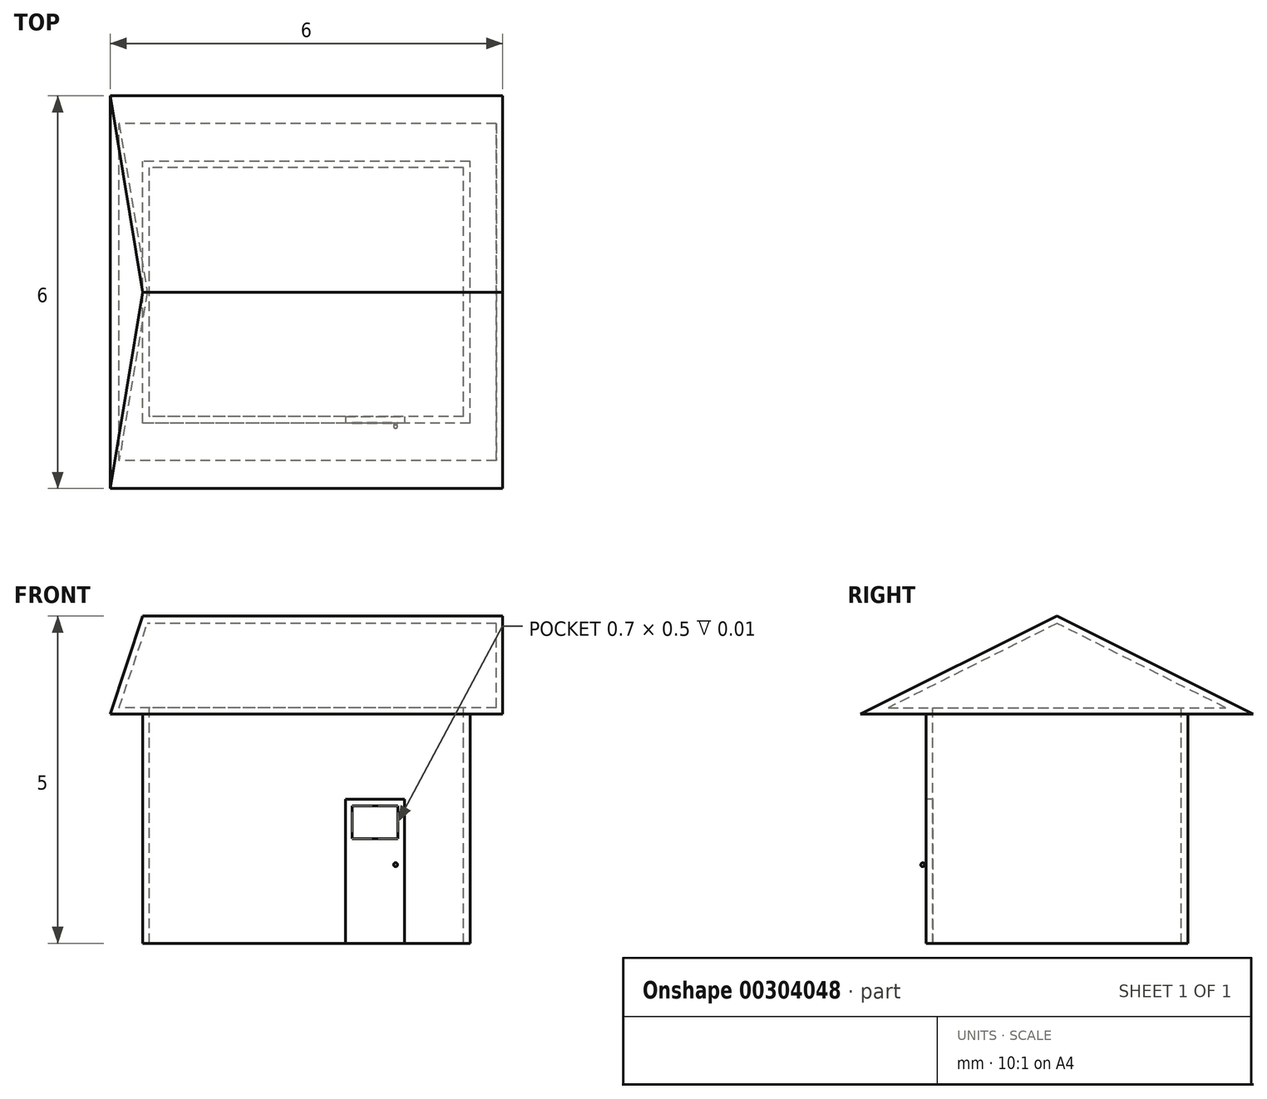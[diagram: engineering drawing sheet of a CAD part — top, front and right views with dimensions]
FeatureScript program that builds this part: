
annotation { "Feature Type Name" : "Feature", "Feature Type Description" : "" }
export const myFeature = defineFeature(function(context is Context, id is Id, definition is map)
    precondition{}
    {
        {
            var Q0;
            Q0=qCreatedBy(makeId("Front.planeOp"),FACE);
            var sketch = newSketch(context, id + "F0", { "sketchPlane" : qUnion([Q0])});
            skLineSegment(sketch, "E0.bottom", {"start": v(2.5, 0) * mm, "end": v(-2.5, 0) * mm});
            skLineSegment(sketch, "E0.top", {"start": v(2.5, 3.5) * mm, "end": v(-2.5, 3.5) * mm});
            skLineSegment(sketch, "E0.left", {"start": v(2.5, 0) * mm, "end": v(2.5, 3.5) * mm});
            skLineSegment(sketch, "E0.right", {"start": v(-2.5, 0) * mm, "end": v(-2.5, 3.5) * mm});
            skPoint(sketch, "E0.middle", {"position": v(0, 1.75) * mm});
            skSolve(sketch);
        }
        {
            var Q0;
            Q0=makeQuery(id+"F0.imprint","IMPRINT",FACE,{"disambiguationData":[TD([[makeQuery(id+"F0.imprint","IMPRINT",EDGE,{"derivedFrom":sQuery(id+"F0.wireOp",EDGE,"E0.bottom")}),-1.0]])]});
            extrude(context, id + "F1", {"entities" : qUnion([Q0]), "depth" : 4 * mm});
        }
        {
            var Q0;
            Q0=makeQuery(id+"F1.opExtrude","CAP_FACE",FACE,{"disambiguationData":[OSD([sQuery(id+"F0.wireOp",EDGE,"E0.bottom"),sQuery(id+"F0.wireOp",EDGE,"E0.top"),sQuery(id+"F0.wireOp",EDGE,"E0.left"),sQuery(id+"F0.wireOp",EDGE,"E0.right")])],"isStart":false});
            var sketch = newSketch(context, id + "F2", { "sketchPlane" : qUnion([Q0])});
            skLineSegment(sketch, "E1.bottom", {"start": v(1.5, 0) * mm, "end": v(0.6, 0) * mm});
            skLineSegment(sketch, "E1.top", {"start": v(1.5, 2.2) * mm, "end": v(0.6, 2.2) * mm});
            skLineSegment(sketch, "E1.left", {"start": v(1.5, 0) * mm, "end": v(1.5, 2.2) * mm});
            skLineSegment(sketch, "E1.right", {"start": v(0.6, 0) * mm, "end": v(0.6, 2.2) * mm});
            skPoint(sketch, "E1.middle", {"position": v(1.05, 1.1) * mm});
            skSolve(sketch);
        }
        {
            var Q0;
            Q0=makeQuery(id+"F1.opExtrude","SWEPT_FACE",FACE,{"disambiguationData":[OSD([sQuery(id+"F0.wireOp",EDGE,"E0.left")])]});
            var sketch = newSketch(context, id + "F3", { "sketchPlane" : qUnion([Q0])});
            skLineSegment(sketch, "E2", {"start": v(-5, 3.5) * mm, "end": v(1, 3.5) * mm});
            skLineSegment(sketch, "E3", {"start": v(1, 3.5) * mm, "end": v(-2, 5) * mm});
            skLineSegment(sketch, "E4", {"start": v(-2, 5) * mm, "end": v(-5, 3.5) * mm});
            skSolve(sketch);
        }
        {
            var Q0;
            {var subQ0=sQuery(id+"F3.wireOp",EDGE,"E3");Q0=makeQuery(id+"F3.imprint","IMPRINT",FACE,{"disambiguationData":[TD([[makeQuery(id+"F3.imprint","IMPRINT",EDGE,{"derivedFrom":subQ0}),1.0]])]});}
            extrude(context, id + "F4", {"entities" : qUnion([Q0]), "operationType" : NewBodyOperationType.ADD, "depth" : 0.5 * mm, "hasSecondDirection" : true, "secondDirectionOppositeDirection" : true, "secondDirectionDepth" : 5.5 * mm});
        }
        {
            var Q0;
            Q0=makeQuery(id+"F2.imprint","IMPRINT",FACE,{"disambiguationData":[TD([[makeQuery(id+"F2.imprint","IMPRINT",EDGE,{"derivedFrom":sQuery(id+"F2.wireOp",EDGE,"E1.top")}),-1.0]])]});
            var sketch = newSketch(context, id + "F5", { "sketchPlane" : qUnion([Q0])});
            skLineSegment(sketch, "E5", {"start": v(-3, 3.5) * mm, "end": v(-2.5, 5) * mm});
            skLineSegment(sketch, "E6", {"start": v(-2.5, 5) * mm, "end": v(-3, 5) * mm});
            skLineSegment(sketch, "E7", {"start": v(-3, 5) * mm, "end": v(-3, 3.5) * mm});
            skSolve(sketch);
        }
        {
            var Q0;
            Q0 = qSketchRegion(id + "F5", true);
            extrude(context, id + "F6", {"entities" : qUnion([Q0]), "operationType" : NewBodyOperationType.REMOVE, "oppositeDirection" : true, "depth" : 25 * mm, "hasSecondDirection" : true, "secondDirectionOppositeDirection" : false, "secondDirectionDepth" : 25 * mm});
        }
        {
            var Q0;
            Q0=makeQuery(id+"F1.opExtrude","SWEPT_FACE",FACE,{"disambiguationData":[OSD([sQuery(id+"F0.wireOp",EDGE,"E0.bottom")])]});
            shell(context, id + "F7", {"entities" : qUnion([Q0]), "thickness" : 0.1 * mm});
        }
        {
            var Q0;
            Q0=makeQuery(id+"F2.imprint","IMPRINT",FACE,{"disambiguationData":[TD([[makeQuery(id+"F2.imprint","IMPRINT",EDGE,{"derivedFrom":sQuery(id+"F2.wireOp",EDGE,"E1.bottom")}),-1.0]])]});
            extrude(context, id + "F8", {"entities" : qUnion([Q0]), "operationType" : NewBodyOperationType.REMOVE, "endBound" : BoundingType.UP_TO_NEXT, "oppositeDirection" : true, "depth" : 25 * mm});
        }
        {
            var Q0;
            Q0=makeQuery(id+"F1.opExtrude","CAP_FACE",FACE,{"disambiguationData":[OSD([sQuery(id+"F0.wireOp",EDGE,"E0.bottom"),sQuery(id+"F0.wireOp",EDGE,"E0.top"),sQuery(id+"F0.wireOp",EDGE,"E0.left"),sQuery(id+"F0.wireOp",EDGE,"E0.right")])],"isStart":false});
            var sketch = newSketch(context, id + "F9", { "sketchPlane" : qUnion([Q0])});
            skLineSegment(sketch, "E8.bottom", {"start": v(0.6, 0) * mm, "end": v(1.5, 0) * mm});
            skLineSegment(sketch, "E8.top", {"start": v(0.6, 2.2) * mm, "end": v(1.5, 2.2) * mm});
            skLineSegment(sketch, "E8.left", {"start": v(0.6, 0) * mm, "end": v(0.6, 2.2) * mm});
            skLineSegment(sketch, "E8.right", {"start": v(1.5, 0) * mm, "end": v(1.5, 2.2) * mm});
            skSolve(sketch);
        }
        {
            var Q0;
            Q0=makeQuery(id+"F9.imprint","IMPRINT",FACE,{"disambiguationData":[TD([[makeQuery(id+"F9.imprint","IMPRINT",EDGE,{"derivedFrom":sQuery(id+"F9.wireOp",EDGE,"E8.bottom")}),1.0]])]});
            extrude(context, id + "F10", {"entities" : qUnion([Q0]), "oppositeDirection" : true, "depth" : 0.1 * mm});
        }
        {
            var Q0;
            Q0=makeQuery(id+"F10.opExtrude","CAP_FACE",FACE,{"disambiguationData":[OSD([sQuery(id+"F9.wireOp",EDGE,"E8.bottom"),sQuery(id+"F9.wireOp",EDGE,"E8.top"),sQuery(id+"F9.wireOp",EDGE,"E8.left"),sQuery(id+"F9.wireOp",EDGE,"E8.right")])],"isStart":true});
            var sketch = newSketch(context, id + "F11", { "sketchPlane" : qUnion([Q0])});
            skLineSegment(sketch, "E9.bottom", {"start": v(0.7, 2.1) * mm, "end": v(1.4, 2.1) * mm});
            skLineSegment(sketch, "E9.top", {"start": v(0.7, 1.6) * mm, "end": v(1.4, 1.6) * mm});
            skLineSegment(sketch, "E9.left", {"start": v(0.7, 2.1) * mm, "end": v(0.7, 1.6) * mm});
            skLineSegment(sketch, "E9.right", {"start": v(1.4, 2.1) * mm, "end": v(1.4, 1.6) * mm});
            skSolve(sketch);
        }
        {
            var Q0;
            Q0=makeQuery(id+"F11.imprint","IMPRINT",FACE,{"disambiguationData":[TD([[makeQuery(id+"F11.imprint","IMPRINT",EDGE,{"derivedFrom":sQuery(id+"F11.wireOp",EDGE,"E9.bottom")}),-1.0]])]});
            extrude(context, id + "F12", {"entities" : qUnion([Q0]), "operationType" : NewBodyOperationType.REMOVE, "oppositeDirection" : true, "depth" : 0.01 * mm});
        }
        {
            var Q0;
            Q0=makeQuery(id+"F10.opExtrude","SWEPT_FACE",FACE,{"disambiguationData":[OSD([sQuery(id+"F9.wireOp",EDGE,"E8.bottom")])]});
            cPlane(context, id + "F13", {"entities" : qUnion([Q0]), "cplaneType" : CPlaneType.OFFSET, "offset" : 1.2 * mm, "oppositeDirection" : true, "width" : 150 * mm, "height" : 150 * mm});
        }
        {
            var Q0;
            Q0=qCreatedBy(id+"F13.planeOp",FACE);
            var sketch = newSketch(context, id + "F14", { "sketchPlane" : qUnion([Q0])});
            skArc(sketch, "E10", {"start": v(1.38, 4.03) * mm, "mid": v(1.4, 4.06) * mm, "end": v(1.36, 4.08) * mm});
            skLineSegment(sketch, "E11", {"start": v(1.36, 4.02) * mm, "end": v(1.36, 4) * mm});
            skLineSegment(sketch, "E12", {"start": v(1.36, 4) * mm, "end": v(1.38, 4) * mm});
            skLineSegment(sketch, "E13", {"start": v(1.38, 4) * mm, "end": v(1.38, 4.03) * mm});
            skLineSegment(sketch, "E14", {"start": v(1.36, 4.02) * mm, "end": v(1.36, 4.08) * mm});
            skSolve(sketch);
        }
        {
            var Q0;
            Q0=makeQuery(id+"F14.imprint","IMPRINT",FACE,{"disambiguationData":[TD([[makeQuery(id+"F14.imprint","IMPRINT",EDGE,{"derivedFrom":sQuery(id+"F14.wireOp",EDGE,"E10")}),1.0]])]});
            var Q1;
            Q1=sQuery(id+"F14.wireOp",EDGE,"E14");
            revolve(context, id + "F15", {"operationType" : NewBodyOperationType.ADD, "entities" : qUnion([Q0]), "axis" : qUnion([Q1]), "revolveType" : RevolveType.FULL});
        }
    });
